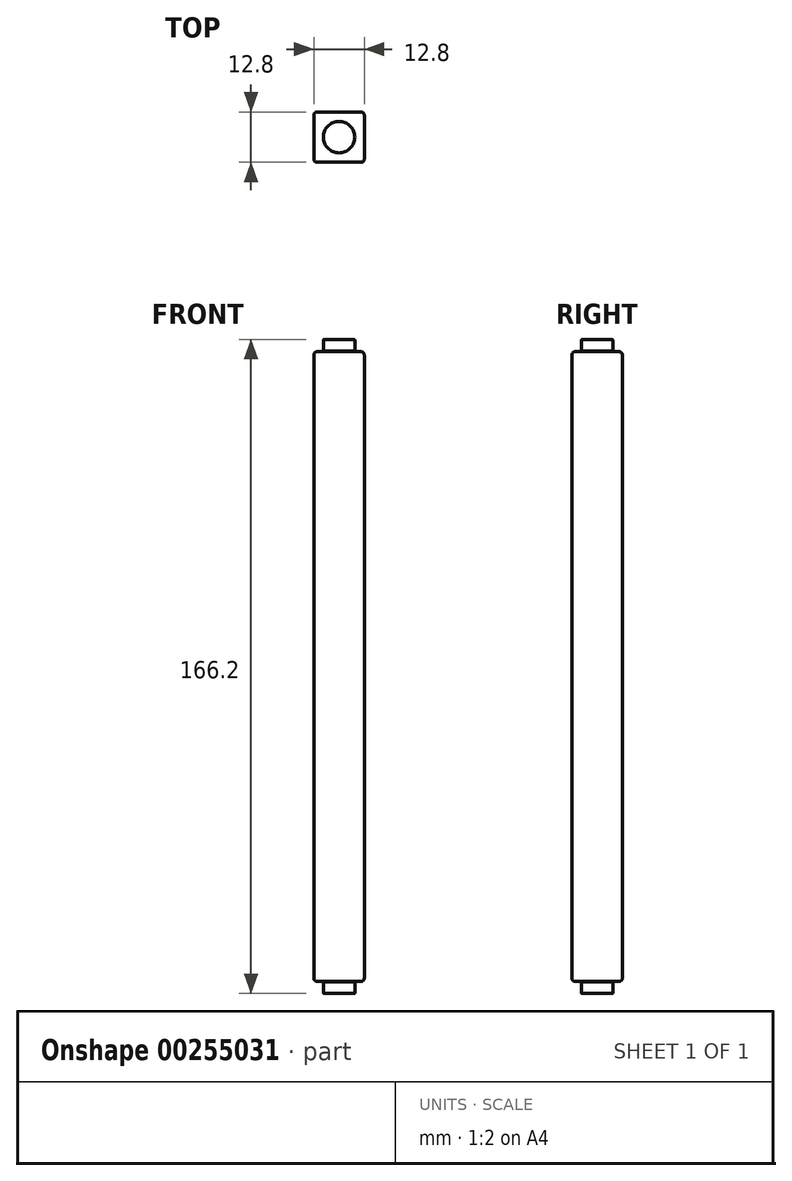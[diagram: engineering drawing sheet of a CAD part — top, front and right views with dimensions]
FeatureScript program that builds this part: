
annotation { "Feature Type Name" : "Feature", "Feature Type Description" : "" }
export const myFeature = defineFeature(function(context is Context, id is Id, definition is map)
    precondition{}
    {
        {
            var Q0;
            Q0=qCreatedBy(makeId("Top.planeOp"),FACE);
            var sketch = newSketch(context, id + "F0", { "sketchPlane" : qUnion([Q0])});
            skLineSegment(sketch, "E0.bottom", {"start": v(6.4, -6.4) * mm, "end": v(-6.4, -6.4) * mm});
            skLineSegment(sketch, "E0.top", {"start": v(6.4, 6.4) * mm, "end": v(-6.4, 6.4) * mm});
            skLineSegment(sketch, "E0.left", {"start": v(6.4, -6.4) * mm, "end": v(6.4, 6.4) * mm});
            skLineSegment(sketch, "E0.right", {"start": v(-6.4, -6.4) * mm, "end": v(-6.4, 6.4) * mm});
            skPoint(sketch, "E0.middle", {"position": v(0, 0) * mm});
            skSolve(sketch);
        }
        {
            var Q0;
            Q0 = qSketchRegion(id + "F0", true);
            extrude(context, id + "F1", {"entities" : qUnion([Q0]), "depth" : 160 * mm});
        }
        {
            var Q0;
            Q0=makeQuery(id+"F1.opExtrude","SWEPT_EDGE",EDGE,{"disambiguationData":[OSD([sQuery(id+"F0.wireOp",EDGE,"E0.bottom"),sQuery(id+"F0.wireOp",EDGE,"E0.left")])]});
            var Q1;
            Q1=makeQuery(id+"F1.opExtrude","SWEPT_EDGE",EDGE,{"disambiguationData":[OSD([sQuery(id+"F0.wireOp",EDGE,"E0.bottom"),sQuery(id+"F0.wireOp",EDGE,"E0.right")])]});
            var Q2;
            Q2=makeQuery(id+"F1.opExtrude","SWEPT_EDGE",EDGE,{"disambiguationData":[OSD([sQuery(id+"F0.wireOp",EDGE,"E0.top"),sQuery(id+"F0.wireOp",EDGE,"E0.left")])]});
            var Q3;
            Q3=makeQuery(id+"F1.opExtrude","SWEPT_EDGE",EDGE,{"disambiguationData":[OSD([sQuery(id+"F0.wireOp",EDGE,"E0.top"),sQuery(id+"F0.wireOp",EDGE,"E0.right")])]});
            var Q4;
            Q4=makeQuery(id+"F1.opExtrude","CAP_FACE",FACE,{"disambiguationData":[OSD([sQuery(id+"F0.wireOp",EDGE,"E0.bottom"),sQuery(id+"F0.wireOp",EDGE,"E0.top"),sQuery(id+"F0.wireOp",EDGE,"E0.left"),sQuery(id+"F0.wireOp",EDGE,"E0.right")])],"isStart":true});
            var Q5;
            Q5=makeQuery(id+"F1.opExtrude","CAP_FACE",FACE,{"disambiguationData":[OSD([sQuery(id+"F0.wireOp",EDGE,"E0.bottom"),sQuery(id+"F0.wireOp",EDGE,"E0.top"),sQuery(id+"F0.wireOp",EDGE,"E0.left"),sQuery(id+"F0.wireOp",EDGE,"E0.right")])],"isStart":false});
            fillet(context, id + "F2", {"entities" : qUnion([Q0, Q1, Q2, Q3, Q4, Q5]), "radius" : 0.8 * mm, "tangentPropagation" : true, "allowEdgeOverflow" : false});
        }
        {
            var Q0;
            Q0=makeQuery(id+"F1.opExtrude","CAP_FACE",FACE,{"disambiguationData":[OSD([sQuery(id+"F0.wireOp",EDGE,"E0.bottom"),sQuery(id+"F0.wireOp",EDGE,"E0.top"),sQuery(id+"F0.wireOp",EDGE,"E0.left"),sQuery(id+"F0.wireOp",EDGE,"E0.right")])],"isStart":true});
            var sketch = newSketch(context, id + "F3", { "sketchPlane" : qUnion([Q0])});
            skCircle(sketch, "E1", {"center": v(0, 0) * mm, "radius": 4 * mm});
            skSolve(sketch);
        }
        {
            var Q0;
            Q0 = qSketchRegion(id + "F3", true);
            extrude(context, id + "F4", {"entities" : qUnion([Q0]), "depth" : 3.1 * mm, "hasSecondDirection" : true, "secondDirectionOppositeDirection" : false, "secondDirectionDepth" : 0.1 * mm});
        }
        {
            var Q0;
            Q0=makeQuery(id+"F4.opExtrude","CAP_EDGE",EDGE,{"disambiguationData":[OSD([sQuery(id+"F3.wireOp",EDGE,"E1")])],"isStart":false});
            var Q1;
            Q1=makeQuery(id+"F4.opExtrude","CAP_EDGE",EDGE,{"disambiguationData":[OSD([sQuery(id+"F3.wireOp",EDGE,"E1")])],"isStart":true});
            fillet(context, id + "F5", {"entities" : qUnion([Q0, Q1]), "radius" : 0.2 * mm, "tangentPropagation" : true, "allowEdgeOverflow" : false});
        }
        {
            var Q0;
            Q0=makeQuery(id+"F1.opExtrude","CAP_FACE",FACE,{"disambiguationData":[OSD([sQuery(id+"F0.wireOp",EDGE,"E0.bottom"),sQuery(id+"F0.wireOp",EDGE,"E0.top"),sQuery(id+"F0.wireOp",EDGE,"E0.left"),sQuery(id+"F0.wireOp",EDGE,"E0.right")])],"isStart":false});
            var sketch = newSketch(context, id + "F6", { "sketchPlane" : qUnion([Q0])});
            skCircle(sketch, "E2", {"center": v(0, 0) * mm, "radius": 4 * mm});
            skSolve(sketch);
        }
        {
            var Q0;
            Q0 = qSketchRegion(id + "F6", true);
            extrude(context, id + "F7", {"entities" : qUnion([Q0]), "depth" : 3.1 * mm, "hasSecondDirection" : true, "secondDirectionOppositeDirection" : false, "secondDirectionDepth" : 0.1 * mm});
        }
        {
            var Q0;
            Q0=makeQuery(id+"F7.opExtrude","CAP_EDGE",EDGE,{"disambiguationData":[OSD([sQuery(id+"F6.wireOp",EDGE,"E2")])],"isStart":false});
            var Q1;
            Q1=makeQuery(id+"F7.opExtrude","CAP_EDGE",EDGE,{"disambiguationData":[OSD([sQuery(id+"F6.wireOp",EDGE,"E2")])],"isStart":true});
            fillet(context, id + "F8", {"entities" : qUnion([Q0, Q1]), "radius" : 0.2 * mm, "tangentPropagation" : true, "allowEdgeOverflow" : false});
        }
    });
